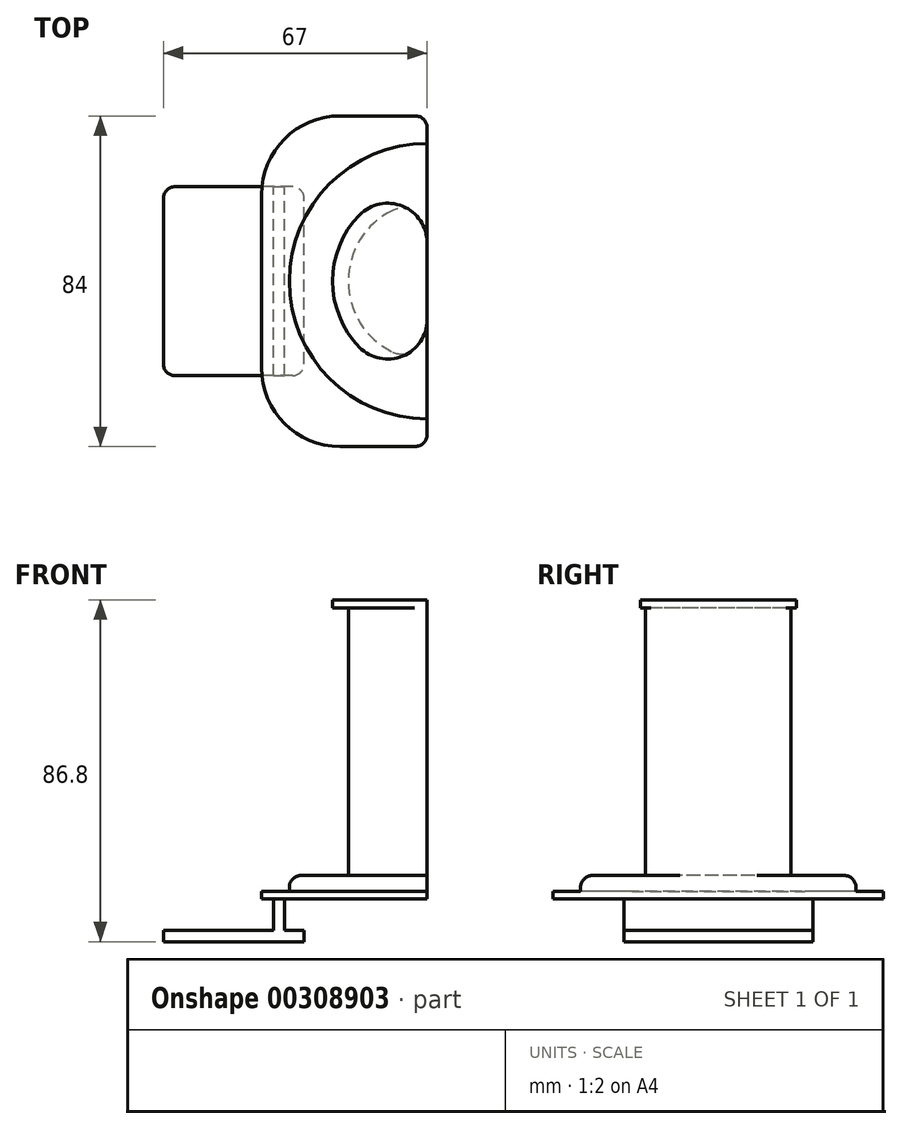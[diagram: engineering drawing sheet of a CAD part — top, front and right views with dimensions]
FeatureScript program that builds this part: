
annotation { "Feature Type Name" : "Feature", "Feature Type Description" : "" }
export const myFeature = defineFeature(function(context is Context, id is Id, definition is map)
    precondition{}
    {
        {
            var Q0;
            Q0=qCreatedBy(makeId("Top.planeOp"),FACE);
            var sketch = newSketch(context, id + "F0", { "sketchPlane" : qUnion([Q0])});
            skCircle(sketch, "E0", {"center": v(0, 0) * mm, "radius": 42 * mm});
            skCircle(sketch, "E1", {"center": v(0, 0) * mm, "radius": 35 * mm});
            skCircle(sketch, "E2", {"center": v(0, 0) * mm, "radius": 20 * mm});
            skLineSegment(sketch, "E3", {"start": v(0, -20) * mm, "end": v(0, 20) * mm});
            skLineSegment(sketch, "E4", {"start": v(0, -42) * mm, "end": v(0, 42) * mm});
            skLineSegment(sketch, "E5.bottom", {"start": v(-22.08, -42) * mm, "end": v(22.08, -42) * mm});
            skLineSegment(sketch, "E5.top", {"start": v(-22.08, 42) * mm, "end": v(22.08, 42) * mm});
            skLineSegment(sketch, "E5.left", {"start": v(-42.08, -22) * mm, "end": v(-42.08, 22) * mm});
            skLineSegment(sketch, "E5.right", {"start": v(42.08, -22) * mm, "end": v(42.08, 22) * mm});
            skPoint(sketch, "E6.visualSharp", {"position": v(-42.08, -42) * mm});
            skArc(sketch, "E6.filletArc", {"start": v(-42.08, -22) * mm, "mid": v(-36.23, -36.14) * mm, "end": v(-22.08, -42) * mm});
            skPoint(sketch, "E7.visualSharp", {"position": v(-42.08, 42) * mm});
            skArc(sketch, "E7.filletArc", {"start": v(-22.08, 42) * mm, "mid": v(-36.23, 36.14) * mm, "end": v(-42.08, 22) * mm});
            skPoint(sketch, "E8.visualSharp", {"position": v(42.08, -42) * mm});
            skArc(sketch, "E8.filletArc", {"start": v(22.08, -42) * mm, "mid": v(36.23, -36.14) * mm, "end": v(42.08, -22) * mm});
            skPoint(sketch, "E9.visualSharp", {"position": v(42.08, 42) * mm});
            skArc(sketch, "E9.filletArc", {"start": v(42.08, 22) * mm, "mid": v(36.23, 36.14) * mm, "end": v(22.08, 42) * mm});
            skSolve(sketch);
        }
        {
            var Q0;
            {var subQ0=sQuery(id+"F0.wireOp",EDGE,"E4");var subQ4=sQuery(id+"F0.wireOp",EDGE,"E1");var subQ6=makeQuery(id+"F0.imprint","INTERSECT",VERTEX,{"disambiguationData":[OD(0.0)],"derivedFrom":[subQ4,subQ0]});Q0=makeQuery(id+"F0.imprint","IMPRINT",FACE,{"disambiguationData":[TD([[makeQuery(id+"F0.imprint","IMPRINT",EDGE,{"disambiguationData":[TD([[subQ6,1.0]])],"derivedFrom":subQ4}),-1.0]])]});}
            var Q1;
            {var subQ0=sQuery(id+"F0.wireOp",EDGE,"E4");var subQ1=sQuery(id+"F0.wireOp",EDGE,"E2");var subQ2=makeQuery(id+"F0.imprint","INTERSECT",VERTEX,{"disambiguationData":[OD(0.0)],"derivedFrom":[subQ1,subQ0]});Q1=makeQuery(id+"F0.imprint","IMPRINT",FACE,{"disambiguationData":[TD([[makeQuery(id+"F0.imprint","IMPRINT",EDGE,{"disambiguationData":[TD([[subQ2,1.0]])],"derivedFrom":subQ1}),1.0]])]});}
            var Q2;
            {var subQ0=sQuery(id+"F0.wireOp",EDGE,"E4");var subQ1=sQuery(id+"F0.wireOp",EDGE,"E1");var subQ2=makeQuery(id+"F0.imprint","INTERSECT",VERTEX,{"disambiguationData":[OD(0.0)],"derivedFrom":[subQ1,subQ0]});Q2=makeQuery(id+"F0.imprint","IMPRINT",FACE,{"disambiguationData":[TD([[makeQuery(id+"F0.imprint","IMPRINT",EDGE,{"disambiguationData":[TD([[subQ2,1.0]])],"derivedFrom":subQ1}),1.0]])]});}
            var Q3;
            Q3=makeQuery(id+"F0.imprint","IMPRINT",FACE,{"disambiguationData":[TD([[makeQuery(id+"F0.imprint","IMPRINT",EDGE,{"derivedFrom":sQuery(id+"F0.wireOp",EDGE,"E5.left")}),-1.0]])]});
            extrude(context, id + "F1", {"entities" : qUnion([Q0, Q1, Q2, Q3]), "depth" : 2 * mm});
        }
        {
            var Q0;
            {var subQ0=sQuery(id+"F0.wireOp",EDGE,"E4");var subQ1=sQuery(id+"F0.wireOp",EDGE,"E1");var subQ2=makeQuery(id+"F0.imprint","INTERSECT",VERTEX,{"disambiguationData":[OD(0.0)],"derivedFrom":[subQ1,subQ0]});Q0=makeQuery(id+"F0.imprint","IMPRINT",FACE,{"disambiguationData":[TD([[makeQuery(id+"F0.imprint","IMPRINT",EDGE,{"disambiguationData":[TD([[subQ2,1.0]])],"derivedFrom":subQ1}),1.0]])]});}
            var Q1;
            {var subQ0=sQuery(id+"F0.wireOp",EDGE,"E4");var subQ1=sQuery(id+"F0.wireOp",EDGE,"E2");var subQ2=makeQuery(id+"F0.imprint","INTERSECT",VERTEX,{"disambiguationData":[OD(0.0)],"derivedFrom":[subQ1,subQ0]});Q1=makeQuery(id+"F0.imprint","IMPRINT",FACE,{"disambiguationData":[TD([[makeQuery(id+"F0.imprint","IMPRINT",EDGE,{"disambiguationData":[TD([[subQ2,1.0]])],"derivedFrom":subQ1}),1.0]])]});}
            extrude(context, id + "F2", {"entities" : qUnion([Q0, Q1]), "operationType" : NewBodyOperationType.ADD, "depth" : 6 * mm});
        }
        {
            var Q0;
            {var subQ0=sQuery(id+"F0.wireOp",EDGE,"E4");var subQ1=sQuery(id+"F0.wireOp",EDGE,"E2");var subQ2=makeQuery(id+"F0.imprint","INTERSECT",VERTEX,{"disambiguationData":[OD(0.0)],"derivedFrom":[subQ1,subQ0]});Q0=makeQuery(id+"F0.imprint","IMPRINT",FACE,{"disambiguationData":[TD([[makeQuery(id+"F0.imprint","IMPRINT",EDGE,{"disambiguationData":[TD([[subQ2,1.0]])],"derivedFrom":subQ1}),1.0]])]});}
            extrude(context, id + "F3", {"entities" : qUnion([Q0]), "operationType" : NewBodyOperationType.ADD, "depth" : 76 * mm});
        }
        {
            var Q0;
            Q0=makeQuery(id+"F3.opExtrude","CAP_FACE",FACE,{"disambiguationData":[OSD([sQuery(id+"F0.wireOp",EDGE,"E2")])],"isStart":false});
            var sketch = newSketch(context, id + "F4", { "sketchPlane" : qUnion([Q0])});
            skCircle(sketch, "E10", {"center": v(0, 0) * mm, "radius": 24 * mm});
            skLineSegment(sketch, "E11", {"start": v(0, 24) * mm, "end": v(0, -24) * mm});
            skSolve(sketch);
        }
        {
            var Q0;
            {var subQ0=sQuery(id+"F4.wireOp",EDGE,"E11");var subQ1=sQuery(id+"F4.wireOp",EDGE,"E10");var subQ2=makeQuery(id+"F4.imprint","INTERSECT",VERTEX,{"disambiguationData":[OD(0.0)],"derivedFrom":[subQ1,subQ0]});Q0=makeQuery(id+"F4.imprint","IMPRINT",FACE,{"disambiguationData":[TD([[makeQuery(id+"F4.imprint","IMPRINT",EDGE,{"disambiguationData":[TD([[subQ2,-1.0]])],"derivedFrom":subQ1}),1.0]])]});}
            extrude(context, id + "F5", {"entities" : qUnion([Q0]), "operationType" : NewBodyOperationType.ADD, "oppositeDirection" : true, "depth" : 2 * mm});
        }
        {
            var Q0;
            {var subQ0=sQuery(id+"F4.wireOp",EDGE,"E11");var subQ1=sQuery(id+"F4.wireOp",EDGE,"E10");Q0=makeQuery(id+"F5.opExtrude","SWEPT_EDGE",EDGE,{"disambiguationData":[OSD([subQ1,subQ0]),TDD([makeQuery(id+"F4.imprint","INTERSECT",VERTEX,{"disambiguationData":[OD(0.0)],"derivedFrom":[subQ1,subQ0]})])]});}
            var Q1;
            {var subQ0=sQuery(id+"F4.wireOp",EDGE,"E11");var subQ1=sQuery(id+"F4.wireOp",EDGE,"E10");Q1=makeQuery(id+"F5.opExtrude","SWEPT_EDGE",EDGE,{"disambiguationData":[OSD([subQ1,subQ0]),TDD([makeQuery(id+"F4.imprint","INTERSECT",VERTEX,{"disambiguationData":[OD(1.0)],"derivedFrom":[subQ1,subQ0]})])]});}
            fillet(context, id + "F6", {"entities" : qUnion([Q0, Q1]), "radius" : 10 * mm, "tangentPropagation" : true, "allowEdgeOverflow" : false});
        }
        {
            var Q0;
            {var subQ0=sQuery(id+"F0.wireOp",EDGE,"E4");var subQ1=sQuery(id+"F0.wireOp",EDGE,"E1");var subQ2=makeQuery(id+"F0.imprint","INTERSECT",VERTEX,{"disambiguationData":[OD(0.0)],"derivedFrom":[subQ1,subQ0]});Q0=makeQuery(id+"F0.imprint","IMPRINT",FACE,{"disambiguationData":[TD([[makeQuery(id+"F0.imprint","IMPRINT",EDGE,{"disambiguationData":[TD([[subQ2,1.0]])],"derivedFrom":subQ1}),1.0]])]});}
            var sketch = newSketch(context, id + "F7", { "sketchPlane" : qUnion([Q0])});
            skLineSegment(sketch, "E12.bottom", {"start": v(-39, -24) * mm, "end": v(-36.2, -24) * mm});
            skLineSegment(sketch, "E12.top", {"start": v(-39, 24) * mm, "end": v(-36.2, 24) * mm});
            skLineSegment(sketch, "E12.left", {"start": v(-39, -24) * mm, "end": v(-39, 24) * mm});
            skLineSegment(sketch, "E12.right", {"start": v(-36.2, -24) * mm, "end": v(-36.2, 24) * mm});
            skPoint(sketch, "E12.middle", {"position": v(-37.6, 0) * mm});
            skSolve(sketch);
        }
        {
            var Q0;
            Q0=makeQuery(id+"F7.imprint","IMPRINT",FACE,{"disambiguationData":[TD([[makeQuery(id+"F7.imprint","IMPRINT",EDGE,{"derivedFrom":sQuery(id+"F7.wireOp",EDGE,"E12.bottom")}),1.0]])]});
            extrude(context, id + "F8", {"entities" : qUnion([Q0]), "operationType" : NewBodyOperationType.ADD, "oppositeDirection" : true, "depth" : 8 * mm});
        }
        {
            var Q0;
            Q0=makeQuery(id+"F8.opExtrude","CAP_FACE",FACE,{"disambiguationData":[OSD([sQuery(id+"F7.wireOp",EDGE,"E12.bottom"),sQuery(id+"F7.wireOp",EDGE,"E12.top"),sQuery(id+"F7.wireOp",EDGE,"E12.left"),sQuery(id+"F7.wireOp",EDGE,"E12.right")])],"isStart":false});
            var sketch = newSketch(context, id + "F9", { "sketchPlane" : qUnion([Q0])});
            skLineSegment(sketch, "E13.bottom", {"start": v(-11, 24) * mm, "end": v(-67, 24) * mm});
            skLineSegment(sketch, "E13.top", {"start": v(-11, -24) * mm, "end": v(-67, -24) * mm});
            skLineSegment(sketch, "E13.left", {"start": v(-11, 24) * mm, "end": v(-11, -24) * mm});
            skLineSegment(sketch, "E13.right", {"start": v(-67, 24) * mm, "end": v(-67, -24) * mm});
            skPoint(sketch, "E13.middle", {"position": v(-39, 0) * mm});
            skLineSegment(sketch, "E14", {"start": v(-31.2, 24) * mm, "end": v(-31.2, -24) * mm});
            skSolve(sketch);
        }
        {
            var Q0;
            {var subQ2=sQuery(id+"F9.wireOp",EDGE,"E13.right");Q0=makeQuery(id+"F9.imprint","IMPRINT",FACE,{"disambiguationData":[TD([[makeQuery(id+"F9.imprint","IMPRINT",EDGE,{"derivedFrom":subQ2}),1.0]])]});}
            var Q1;
            {var subQ2=sQuery(id+"F9.wireOp",EDGE,"E14");Q1=makeQuery(id+"F9.imprint","IMPRINT",FACE,{"disambiguationData":[TD([[makeQuery(id+"F9.imprint","IMPRINT",EDGE,{"derivedFrom":subQ2}),-1.0]])]});}
            var Q2;
            {var subQ1=makeQuery(id+"F8.opExtrude","CAP_EDGE",EDGE,{"disambiguationData":[OSD([sQuery(id+"F7.wireOp",EDGE,"E12.left")])],"isStart":false});Q2=makeQuery(id+"F9.imprint","IMPRINT",FACE,{"disambiguationData":[TD([[makeQuery(id+"F9.imprint","IMPRINT",EDGE,{"derivedFrom":subQ1}),1.0]])]});}
            extrude(context, id + "F10", {"entities" : qUnion([Q0, Q1, Q2]), "operationType" : NewBodyOperationType.ADD, "depth" : 2.8 * mm});
        }
        {
            var Q0;
            Q0=makeQuery(id+"F10.opExtrude","SWEPT_EDGE",EDGE,{"disambiguationData":[OSD([sQuery(id+"F9.wireOp",EDGE,"E13.bottom"),sQuery(id+"F9.wireOp",EDGE,"E13.right")])]});
            var Q1;
            Q1=makeQuery(id+"F10.opExtrude","SWEPT_EDGE",EDGE,{"disambiguationData":[OSD([sQuery(id+"F9.wireOp",EDGE,"E13.bottom"),sQuery(id+"F9.wireOp",EDGE,"E14")])]});
            var Q2;
            Q2=makeQuery(id+"F10.opExtrude","SWEPT_EDGE",EDGE,{"disambiguationData":[OSD([sQuery(id+"F9.wireOp",EDGE,"E13.top"),sQuery(id+"F9.wireOp",EDGE,"E13.right")])]});
            var Q3;
            Q3=makeQuery(id+"F10.opExtrude","SWEPT_EDGE",EDGE,{"disambiguationData":[OSD([sQuery(id+"F9.wireOp",EDGE,"E13.top"),sQuery(id+"F9.wireOp",EDGE,"E14")])]});
            var Q4;
            Q4=makeQuery(id+"F1.opExtrude","SWEPT_EDGE",EDGE,{"disambiguationData":[OSD([sQuery(id+"F0.wireOp",EDGE,"E0"),sQuery(id+"F0.wireOp",EDGE,"E4"),sQuery(id+"F0.wireOp",EDGE,"E5.top")])]});
            var Q5;
            Q5=makeQuery(id+"F1.opExtrude","SWEPT_EDGE",EDGE,{"disambiguationData":[OSD([sQuery(id+"F0.wireOp",EDGE,"E0"),sQuery(id+"F0.wireOp",EDGE,"E4"),sQuery(id+"F0.wireOp",EDGE,"E5.bottom")])]});
            var Q6;
            Q6=makeQuery(id+"F2.opExtrude","CAP_EDGE",EDGE,{"disambiguationData":[OSD([sQuery(id+"F0.wireOp",EDGE,"E1")])],"isStart":false});
            fillet(context, id + "F11", {"entities" : qUnion([Q0, Q1, Q2, Q3, Q4, Q5, Q6]), "radius" : 3 * mm, "tangentPropagation" : true, "allowEdgeOverflow" : false});
        }
        {
            var Q0;
            {var subQ0=sQuery(id+"F4.wireOp",EDGE,"E11");var subQ1=sQuery(id+"F4.wireOp",EDGE,"E10");Q0=makeQuery(id+"F6.opFillet","BLEND_EDGE",EDGE,{"blendedFrom":[makeQuery(id+"F5.opExtrude","SWEPT_EDGE",EDGE,{"disambiguationData":[OSD([subQ1,subQ0]),TDD([makeQuery(id+"F4.imprint","INTERSECT",VERTEX,{"disambiguationData":[OD(1.0)],"derivedFrom":[subQ1,subQ0]})])]}),makeQuery(id+"F3.opExtrude","SWEPT_FACE",FACE,{"disambiguationData":[OSD([sQuery(id+"F0.wireOp",EDGE,"E2")])]})],"blendedInto":[makeQuery(id+"F3.opExtrude","SWEPT_FACE",FACE,{"disambiguationData":[OSD([sQuery(id+"F0.wireOp",EDGE,"E2")])]})]});}
            var Q1;
            {var subQ0=sQuery(id+"F4.wireOp",EDGE,"E11");var subQ1=sQuery(id+"F4.wireOp",EDGE,"E10");Q1=makeQuery(id+"F6.opFillet","BLEND_EDGE",EDGE,{"blendedFrom":[makeQuery(id+"F5.opExtrude","SWEPT_EDGE",EDGE,{"disambiguationData":[OSD([subQ1,subQ0]),TDD([makeQuery(id+"F4.imprint","INTERSECT",VERTEX,{"disambiguationData":[OD(0.0)],"derivedFrom":[subQ1,subQ0]})])]}),makeQuery(id+"F3.opExtrude","SWEPT_FACE",FACE,{"disambiguationData":[OSD([sQuery(id+"F0.wireOp",EDGE,"E2")])]})],"blendedInto":[makeQuery(id+"F3.opExtrude","SWEPT_FACE",FACE,{"disambiguationData":[OSD([sQuery(id+"F0.wireOp",EDGE,"E2")])]})]});}
            fillet(context, id + "F12", {"entities" : qUnion([Q0, Q1]), "radius" : 5 * mm, "tangentPropagation" : true, "allowEdgeOverflow" : false});
        }
    });
